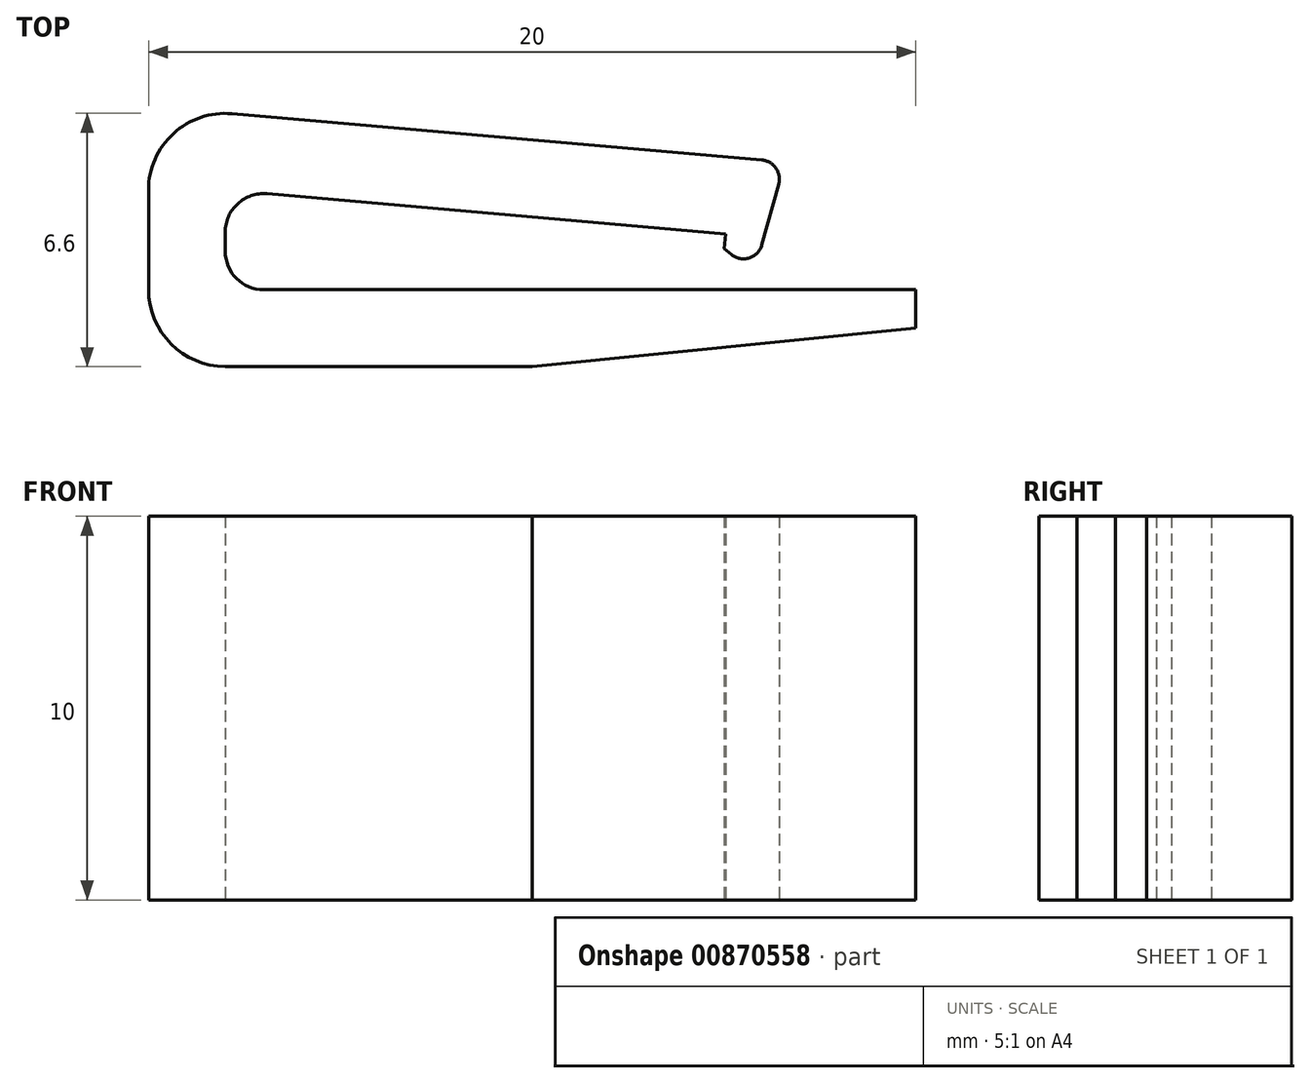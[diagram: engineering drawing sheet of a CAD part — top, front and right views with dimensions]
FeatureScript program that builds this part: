
annotation { "Feature Type Name" : "Feature", "Feature Type Description" : "" }
export const myFeature = defineFeature(function(context is Context, id is Id, definition is map)
    precondition{}
    {
        {
            var Q0;
            Q0=qCreatedBy(makeId("Top.planeOp"),FACE);
            var sketch = newSketch(context, id + "F0", { "sketchPlane" : qUnion([Q0])});
            skLineSegment(sketch, "E0", {"start": v(20, 0.8) * mm, "end": v(3, 0.8) * mm});
            skLineSegment(sketch, "E1", {"start": v(3.09, 3.3) * mm, "end": v(15.04, 2.25) * mm});
            skLineSegment(sketch, "E2", {"start": v(0, 0.8) * mm, "end": v(0, 3.39) * mm});
            skLineSegment(sketch, "E3", {"start": v(2.17, 5.38) * mm, "end": v(15.99, 4.17) * mm});
            skPoint(sketch, "E4.visualSharp", {"position": v(0, 0) * mm});
            skArc(sketch, "E4.filletArc", {"start": v(0, 0.8) * mm, "mid": v(0.59, -0.62) * mm, "end": v(2, -1.2) * mm});
            skPoint(sketch, "E5.visualSharp", {"position": v(0, 5.57) * mm});
            skArc(sketch, "E5.filletArc", {"start": v(2.17, 5.38) * mm, "mid": v(0.65, 4.86) * mm, "end": v(0, 3.39) * mm});
            skLineSegment(sketch, "E6", {"start": v(15.2, 1.71) * mm, "end": v(15, 1.86) * mm});
            skLineSegment(sketch, "E7", {"start": v(15, 1.86) * mm, "end": v(15.04, 2.25) * mm});
            skLineSegment(sketch, "E8", {"start": v(16.43, 3.54) * mm, "end": v(15.99, 1.97) * mm});
            skLineSegment(sketch, "E9", {"start": v(2, -1.2) * mm, "end": v(10, -1.2) * mm});
            skLineSegment(sketch, "E10", {"start": v(10, -1.2) * mm, "end": v(20, -0.2) * mm});
            skLineSegment(sketch, "E11", {"start": v(20, -0.2) * mm, "end": v(20, 0.8) * mm});
            skPoint(sketch, "E12.visualSharp", {"position": v(16.59, 4.12) * mm});
            skArc(sketch, "E12.filletArc", {"start": v(16.43, 3.54) * mm, "mid": v(16.35, 3.96) * mm, "end": v(15.99, 4.17) * mm});
            skPoint(sketch, "E13.visualSharp", {"position": v(15.78, 1.23) * mm});
            skArc(sketch, "E13.filletArc", {"start": v(15.2, 1.71) * mm, "mid": v(15.66, 1.62) * mm, "end": v(15.99, 1.97) * mm});
            skLineSegment(sketch, "E14", {"start": v(2, 2.3) * mm, "end": v(2, 1.8) * mm});
            skArc(sketch, "E15", {"start": v(3.09, 3.3) * mm, "mid": v(2.32, 3.04) * mm, "end": v(2, 2.3) * mm});
            skArc(sketch, "E16", {"start": v(2, 1.8) * mm, "mid": v(2.3, 1.09) * mm, "end": v(3, 0.8) * mm});
            skSolve(sketch);
        }
        {
            var Q0;
            Q0=makeQuery(id+"F0.imprint","IMPRINT",FACE,{"disambiguationData":[TD([[makeQuery(id+"F0.imprint","IMPRINT",EDGE,{"derivedFrom":sQuery(id+"F0.wireOp",EDGE,"E0")}),1.0]])]});
            extrude(context, id + "F1", {"entities" : qUnion([Q0]), "depth" : 10 * mm, "offsetDistance" : 25 * mm});
        }
    });
